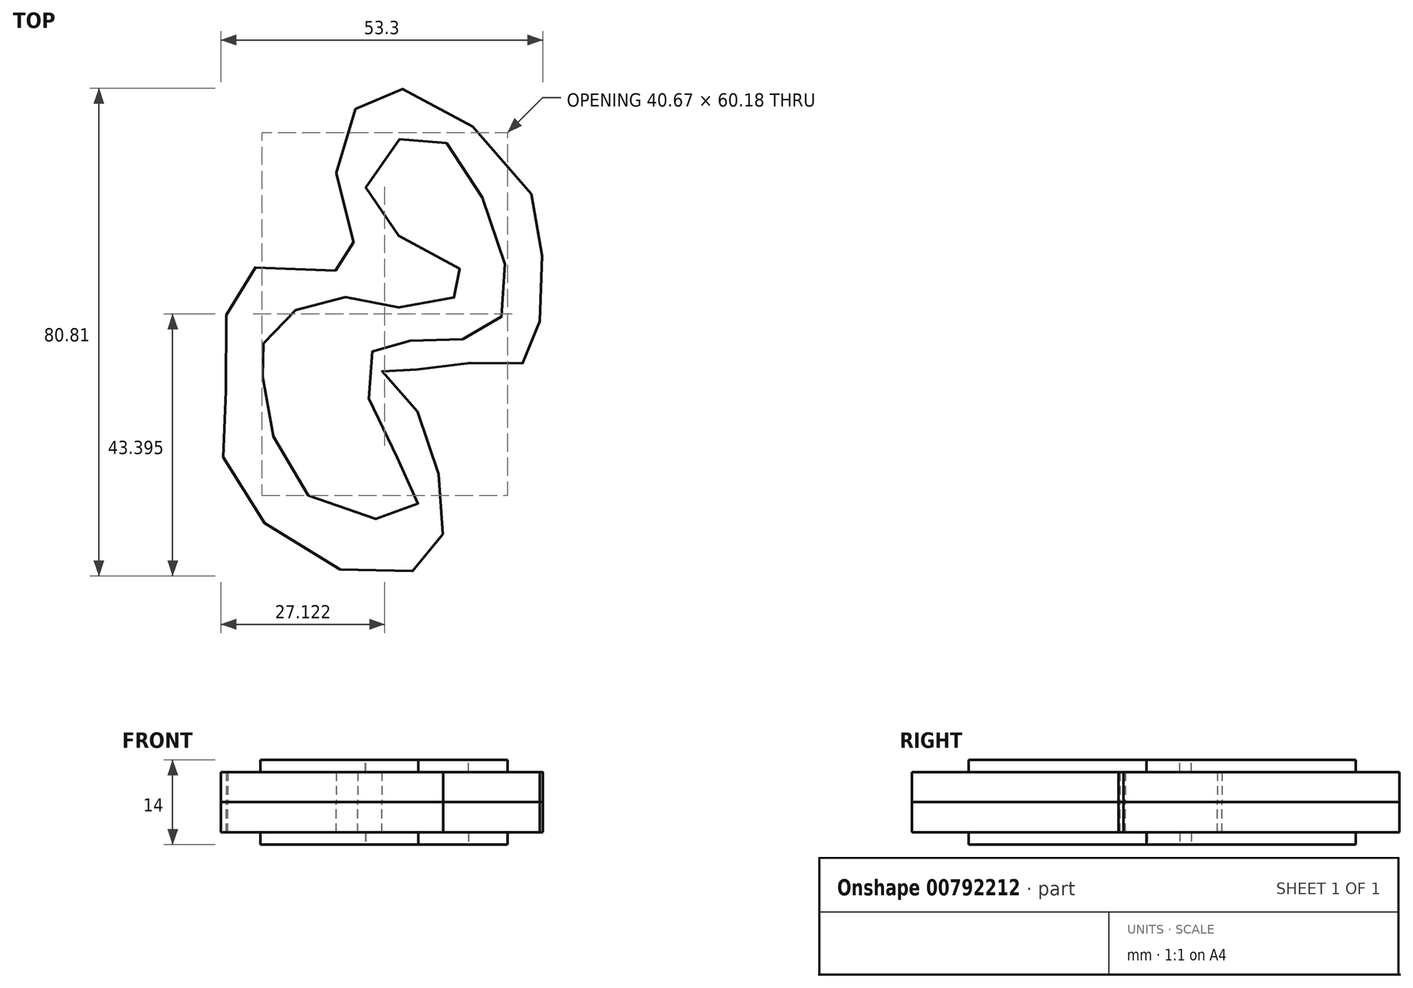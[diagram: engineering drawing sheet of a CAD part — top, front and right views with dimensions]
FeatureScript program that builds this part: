
annotation { "Feature Type Name" : "Feature", "Feature Type Description" : "" }
export const myFeature = defineFeature(function(context is Context, id is Id, definition is map)
    precondition{}
    {
        {
            var Q0;
            Q0=qCreatedBy(makeId("Top.planeOp"),FACE);
            var sketch = newSketch(context, id + "F0", { "sketchPlane" : qUnion([Q0])});
            skFitSpline(sketch, "E0", {"points": [v(-17.87, -40.54) * mm, v(-25.43, -20.78) * mm, v(-25.14, -14.97) * mm, v(-14.97, -7.7) * mm, v(0, -9.44) * mm, v(8.57, -4.5) * mm, v(-8, 7.41) * mm, v(0, 19.61) * mm, v(11.48, 7.7) * mm, v(14.1, -10.9) * mm, v(3.63, -14.97) * mm, v(-6.83, -16.13) * mm, v(-6.25, -28.91) * mm, v(0, -42.57) * mm, v(-17.87, -40.54) * mm]});
            skSolve(sketch);
        }
        {
            var Q0;
            Q0=qCreatedBy(makeId("Top.planeOp"),FACE);
            var sketch = newSketch(context, id + "F1", { "sketchPlane" : qUnion([Q0])});
            skFitSpline(sketch, "E1", {"points": [v(-12.64, -52.74) * mm, v(-31.53, -35.89) * mm, v(-31.24, -19.03) * mm, v(-28.62, -3.34) * mm, v(-10.32, -2.76) * mm, v(-12.64, 7.7) * mm, v(-9.73, 23.97) * mm, v(0, 26.3) * mm, v(19.61, 8.28) * mm, v(20.49, -5.67) * mm, v(19.03, -17.87) * mm, v(10.6, -18.45) * mm, v(0, -19.61) * mm, v(-5.67, -19.61) * mm, v(0, -26.3) * mm, v(4.21, -41.4) * mm, v(2.76, -51) * mm, v(-12.64, -52.74) * mm]});
            skSolve(sketch);
        }
        {
            var Q0;
            Q0=makeQuery(id+"F0.imprint","IMPRINT",FACE,{"disambiguationData":[TD([[makeQuery(id+"F0.imprint","IMPRINT",EDGE,{"derivedFrom":sQuery(id+"F0.wireOp",EDGE,"E0")}),-1.0]])]});
            extrude(context, id + "F2", {"entities" : qUnion([Q0]), "depth" : 7 * mm, "offsetDistance" : 25 * mm});
        }
        {
            var Q0;
            Q0=makeQuery(id+"F1.imprint","IMPRINT",FACE,{"disambiguationData":[TD([[makeQuery(id+"F1.imprint","IMPRINT",EDGE,{"derivedFrom":sQuery(id+"F1.wireOp",EDGE,"E1")}),-1.0]])]});
            extrude(context, id + "F3", {"entities" : qUnion([Q0]), "operationType" : NewBodyOperationType.ADD, "depth" : 5 * mm, "offsetDistance" : 25 * mm});
        }
        {
            var Q0;
            Q0=makeQuery(id+"F2.opExtrude","SWEPT_BODY",BODY,{"disambiguationData":[OSD([sQuery(id+"F0.wireOp",EDGE,"E0")])]});
            var Q1;
            Q1=makeQuery(id+"F3.boolean.opBoolean","MERGE",FACE,{"derivedFrom":[makeQuery(id+"F2.opExtrude","CAP_FACE",FACE,{"disambiguationData":[OSD([sQuery(id+"F0.wireOp",EDGE,"E0")])],"isStart":true}),makeQuery(id+"F3.opExtrude","CAP_FACE",FACE,{"disambiguationData":[OSD([sQuery(id+"F1.wireOp",EDGE,"E1")])],"isStart":true})]});
            mirror(context, id + "F4", {"entities" : qUnion([Q0]), "mirrorPlane" : qUnion([Q1])});
        }
    });
